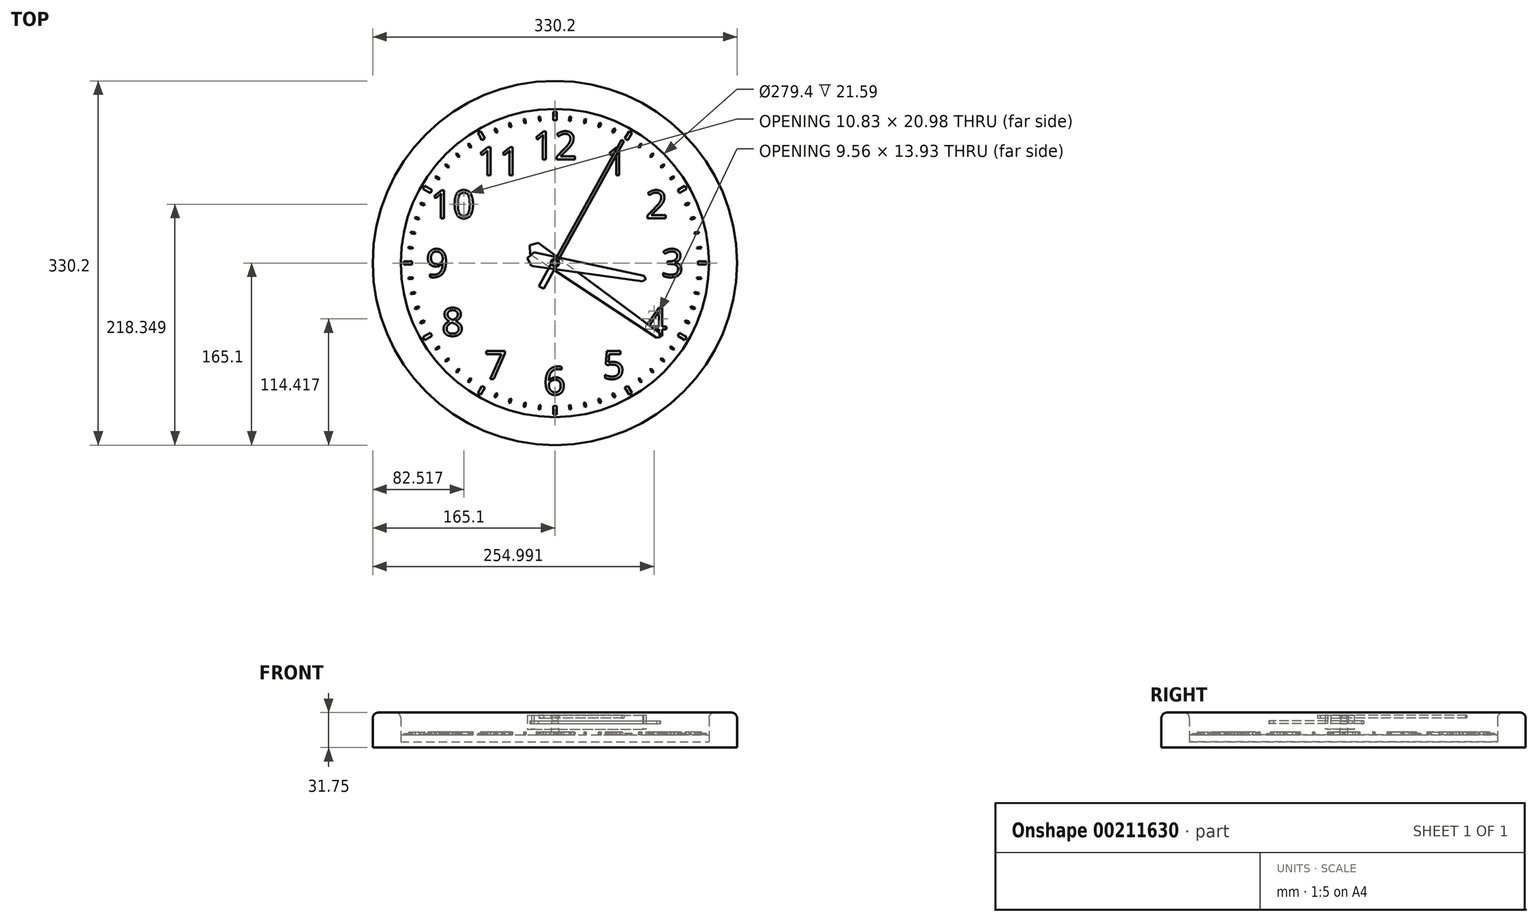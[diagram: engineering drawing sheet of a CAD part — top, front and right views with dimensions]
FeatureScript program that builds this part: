
annotation { "Feature Type Name" : "Feature", "Feature Type Description" : "" }
export const myFeature = defineFeature(function(context is Context, id is Id, definition is map)
    precondition{}
    {
        {
            var Q0;
            Q0=qCreatedBy(makeId("Front.planeOp"),FACE);
            var sketch = newSketch(context, id + "F0", { "sketchPlane" : qUnion([Q0])});
            skLineSegment(sketch, "E0", {"start": v(0, 0) * mm, "end": v(0, 54.8) * mm, "construction": true});
            skLineSegment(sketch, "E1.bottom", {"start": v(139.7, 0) * mm, "end": v(165.1, 0) * mm});
            skLineSegment(sketch, "E1.top", {"start": v(139.7, 31.75) * mm, "end": v(165.1, 31.75) * mm});
            skLineSegment(sketch, "E1.left", {"start": v(139.7, 5.08) * mm, "end": v(139.7, 31.75) * mm});
            skLineSegment(sketch, "E1.right", {"start": v(165.1, 0) * mm, "end": v(165.1, 31.75) * mm});
            skLineSegment(sketch, "E2", {"start": v(152.4, 0) * mm, "end": v(152.4, 31.75) * mm, "construction": true});
            skLineSegment(sketch, "E3.bottom", {"start": v(0, 0) * mm, "end": v(139.7, 0) * mm});
            skLineSegment(sketch, "E3.top", {"start": v(0, 5.08) * mm, "end": v(139.7, 5.08) * mm});
            skLineSegment(sketch, "E3.left", {"start": v(0, 0) * mm, "end": v(0, 5.08) * mm});
            skSolve(sketch);
        }
        {
            var Q0;
            Q0=makeQuery(id+"F0.imprint","IMPRINT",FACE,{"disambiguationData":[TD([[makeQuery(id+"F0.imprint","IMPRINT",EDGE,{"derivedFrom":sQuery(id+"F0.wireOp",EDGE,"E1.bottom")}),1.0]])]});
            var Q1;
            Q1=sQuery(id+"F0.wireOp",EDGE,"E0");
            revolve(context, id + "F1", {"entities" : qUnion([Q0]), "axis" : qUnion([Q1]), "revolveType" : RevolveType.FULL});
        }
        {
            var Q0;
            Q0=makeQuery(id+"F1.opRevolve","SWEPT_EDGE",EDGE,{"disambiguationData":[OSD([sQuery(id+"F0.wireOp",EDGE,"E1.top"),sQuery(id+"F0.wireOp",EDGE,"E1.left")])]});
            var Q1;
            Q1=makeQuery(id+"F1.opRevolve","SWEPT_EDGE",EDGE,{"disambiguationData":[OSD([sQuery(id+"F0.wireOp",EDGE,"E1.top"),sQuery(id+"F0.wireOp",EDGE,"E1.right")])]});
            fillet(context, id + "F2", {"entities" : qUnion([Q0, Q1]), "radius" : 5.08 * mm, "tangentPropagation" : true, "allowEdgeOverflow" : false});
        }
        {
            var Q0;
            Q0=makeQuery(id+"F1.opRevolve","SWEPT_FACE",FACE,{"disambiguationData":[OSD([sQuery(id+"F0.wireOp",EDGE,"E3.top")])]});
            extrude(context, id + "F3", {"entities" : qUnion([Q0]), "depth" : 6.35 * mm});
        }
        {
            var Q0;
            Q0=makeQuery(id+"F3.opExtrude","CAP_FACE",FACE,{"disambiguationData":[OSD([sQuery(id+"F0.wireOp",EDGE,"E3.top")])],"isStart":false});
            var sketch = newSketch(context, id + "F4", { "sketchPlane" : qUnion([Q0])});
            skText(sketch, "E4", { "text": "12", "fontName": "OpenSans-Regular.ttf"});
            skLineSegment(sketch, "E5", {"start": v(0, 0) * mm, "end": v(0, 106.68) * mm, "construction": true});
            skLineSegment(sketch, "E6.1.0", {"start": v(0, 0) * mm, "end": v(-53.34, 92.39) * mm, "construction": true});
            skLineSegment(sketch, "E6.2.0", {"start": v(0, 0) * mm, "end": v(-92.39, 53.34) * mm, "construction": true});
            skLineSegment(sketch, "E6.3.0", {"start": v(0, 0) * mm, "end": v(-106.68, 0) * mm, "construction": true});
            skLineSegment(sketch, "E6.4.0", {"start": v(0, 0) * mm, "end": v(-92.39, -53.34) * mm, "construction": true});
            skLineSegment(sketch, "E6.5.0", {"start": v(0, 0) * mm, "end": v(-53.34, -92.39) * mm, "construction": true});
            skLineSegment(sketch, "E6.6.0", {"start": v(0, 0) * mm, "end": v(0, -106.68) * mm, "construction": true});
            skLineSegment(sketch, "E6.7.0", {"start": v(0, 0) * mm, "end": v(53.34, -92.39) * mm, "construction": true});
            skLineSegment(sketch, "E6.8.0", {"start": v(0, 0) * mm, "end": v(92.39, -53.34) * mm, "construction": true});
            skLineSegment(sketch, "E6.9.0", {"start": v(0, 0) * mm, "end": v(106.68, 0) * mm, "construction": true});
            skLineSegment(sketch, "E6.10.0", {"start": v(0, 0) * mm, "end": v(92.39, 53.34) * mm, "construction": true});
            skLineSegment(sketch, "E6.11.0", {"start": v(0, 0) * mm, "end": v(53.34, 92.39) * mm, "construction": true});
            skPoint(sketch, "E6.center", {"position": v(0, 0) * mm});
            skText(sketch, "E7", { "text": "2", "fontName": "OpenSans-Regular.ttf"});
            skText(sketch, "E8", { "text": "3", "fontName": "OpenSans-Regular.ttf"});
            skText(sketch, "E9", { "text": "4", "fontName": "OpenSans-Regular.ttf"});
            skText(sketch, "E10", { "text": "1", "fontName": "OpenSans-Regular.ttf"});
            skText(sketch, "E11", { "text": "5", "fontName": "OpenSans-Regular.ttf"});
            skText(sketch, "E12", { "text": "6", "fontName": "OpenSans-Regular.ttf"});
            skText(sketch, "E13", { "text": "7", "fontName": "OpenSans-Regular.ttf"});
            skText(sketch, "E14", { "text": "9", "fontName": "OpenSans-Regular.ttf"});
            skText(sketch, "E15", { "text": "8", "fontName": "OpenSans-Regular.ttf"});
            skText(sketch, "E16", { "text": "10", "fontName": "OpenSans-Regular.ttf"});
            skText(sketch, "E17", { "text": "11", "fontName": "OpenSans-Regular.ttf"});
            const initialGuessF4  = {"E4": [-0.02037, 0.09398, 1, 0, 0.0254], "E7": [0.0821, 0.04064, 1, 0, 0.0254], "E8": [0.09649, -0.0127, 1, 0, 0.0254], "E9": [0.08151, -0.06604, 1, 0, 0.0254], "E10": [0.04604, 0.07969, 1, 0, 0.0254], "E11": [0.04313, -0.10509, 1, 0, 0.0254], "E12": [-0.01037, -0.11938, 1, 0, 0.0254], "E13": [-0.06367, -0.10509, 1, 0, 0.0254], "E14": [-0.11696, -0.0127, 1, 0, 0.0254], "E15": [-0.1027, -0.06604, 1, 0, 0.0254], "E16": [-0.11282, 0.04064, 1, 0, 0.0254], "E17": [-0.07073, 0.07969, 1, 0, 0.0254]};
            skSetInitialGuess(sketch, initialGuessF4);
            skSolve(sketch);
        }
        {
            var Q0;
            Q0=qSketchRegion(id+"F4",true);
            extrude(context, id + "F5", {"entities" : qUnion([Q0]), "depth" : 2.54 * mm});
        }
        {
            var Q0;
            Q0=makeQuery(id+"F3.opExtrude","CAP_FACE",FACE,{"disambiguationData":[OSD([sQuery(id+"F0.wireOp",EDGE,"E3.top")])],"isStart":false});
            cPlane(context, id + "F6", {"entities" : qUnion([Q0]), "cplaneType" : CPlaneType.OFFSET, "offset" : 5.08 * mm, "width" : 152.4 * mm, "height" : 152.4 * mm});
        }
        {
            var Q0;
            Q0=qCreatedBy(id+"F6.planeOp",FACE);
            var sketch = newSketch(context, id + "F7", { "sketchPlane" : qUnion([Q0])});
            skLineSegment(sketch, "E18", {"start": v(5, -0.88) * mm, "end": v(80.05, -14.11) * mm, "construction": true});
            skLineSegment(sketch, "E19", {"start": v(80.05, -14.11) * mm, "end": v(79.6, -16.62) * mm, "construction": true});
            skLineSegment(sketch, "E20", {"start": v(-20.01, 3.53) * mm, "end": v(-21.11, -2.72) * mm, "construction": true});
            skLineSegment(sketch, "E21", {"start": v(5, -0.88) * mm, "end": v(-25.01, 4.41) * mm, "construction": true});
            skLineSegment(sketch, "E22", {"start": v(-25.01, 4.41) * mm, "end": v(-21.11, -2.72) * mm});
            skLineSegment(sketch, "E23", {"start": v(-21.11, -2.72) * mm, "end": v(79.6, -16.62) * mm});
            skLineSegment(sketch, "E24", {"start": v(80.05, -14.11) * mm, "end": v(82.55, -14.56) * mm, "construction": true});
            skLineSegment(sketch, "E25", {"start": v(82.55, -14.56) * mm, "end": v(79.6, -16.62) * mm});
            skLineSegment(sketch, "E26.MirrorCS", {"start": v(82.55, -14.56) * mm, "end": v(80.49, -11.61) * mm});
            skLineSegment(sketch, "E27.MirrorCS", {"start": v(-18.9, 9.78) * mm, "end": v(80.49, -11.61) * mm});
            skLineSegment(sketch, "E28.MirrorCS", {"start": v(-25.01, 4.41) * mm, "end": v(-18.9, 9.78) * mm});
            skSolve(sketch);
        }
        {
            var Q0;
            Q0=makeQuery(id+"F7.imprint","IMPRINT",FACE,{"disambiguationData":[TD([[makeQuery(id+"F7.imprint","IMPRINT",EDGE,{"derivedFrom":sQuery(id+"F7.wireOp",EDGE,"E22")}),1.0]])]});
            extrude(context, id + "F8", {"entities" : qUnion([Q0]), "depth" : 12.7 * mm});
        }
        {
            var Q0;
            Q0=makeQuery(id+"F3.opExtrude","CAP_FACE",FACE,{"disambiguationData":[OSD([sQuery(id+"F0.wireOp",EDGE,"E3.top")])],"isStart":false});
            cPlane(context, id + "F9", {"entities" : qUnion([Q0]), "cplaneType" : CPlaneType.OFFSET, "offset" : 10.16 * mm, "width" : 152.4 * mm, "height" : 152.4 * mm});
        }
        {
            var Q0;
            Q0=qCreatedBy(id+"F9.planeOp",FACE);
            var sketch = newSketch(context, id + "F10", { "sketchPlane" : qUnion([Q0])});
            skLineSegment(sketch, "E29", {"start": v(0, 0) * mm, "end": v(95.7, -67.02) * mm, "construction": true});
            skLineSegment(sketch, "E30", {"start": v(0, 0) * mm, "end": v(-22.89, 16.03) * mm, "construction": true});
            skLineSegment(sketch, "E31", {"start": v(-18.73, 13.11) * mm, "end": v(-15.08, 18.31) * mm, "construction": true});
            skLineSegment(sketch, "E32", {"start": v(93.63, -65.56) * mm, "end": v(95.09, -63.48) * mm, "construction": true});
            skLineSegment(sketch, "E33", {"start": v(-22.89, 16.03) * mm, "end": v(-15.08, 18.31) * mm});
            skLineSegment(sketch, "E34", {"start": v(-15.08, 18.31) * mm, "end": v(95.09, -63.48) * mm});
            skLineSegment(sketch, "E35", {"start": v(95.09, -63.48) * mm, "end": v(95.7, -67.02) * mm});
            skLineSegment(sketch, "E36.MirrorCS", {"start": v(-22.89, 16.03) * mm, "end": v(-22.37, 7.91) * mm});
            skLineSegment(sketch, "E37.MirrorCS", {"start": v(-22.37, 7.91) * mm, "end": v(92.17, -67.64) * mm});
            skLineSegment(sketch, "E38.MirrorCS", {"start": v(92.17, -67.64) * mm, "end": v(95.7, -67.02) * mm});
            skLineSegment(sketch, "E39", {"start": v(0, 0) * mm, "end": v(0, -35.35) * mm, "construction": true});
            skSolve(sketch);
        }
        {
            var Q0;
            Q0=makeQuery(id+"F10.imprint","IMPRINT",FACE,{"disambiguationData":[TD([[makeQuery(id+"F10.imprint","IMPRINT",EDGE,{"derivedFrom":sQuery(id+"F10.wireOp",EDGE,"E33")}),-1.0]])]});
            extrude(context, id + "F11", {"entities" : qUnion([Q0]), "depth" : 2.54 * mm});
        }
        {
            var Q0;
            Q0=makeQuery(id+"F3.opExtrude","CAP_FACE",FACE,{"disambiguationData":[OSD([sQuery(id+"F0.wireOp",EDGE,"E3.top")])],"isStart":false});
            cPlane(context, id + "F12", {"entities" : qUnion([Q0]), "cplaneType" : CPlaneType.OFFSET, "offset" : 15.24 * mm, "width" : 152.4 * mm, "height" : 152.4 * mm});
        }
        {
            var Q0;
            Q0=qCreatedBy(id+"F12.planeOp",FACE);
            var sketch = newSketch(context, id + "F13", { "sketchPlane" : qUnion([Q0])});
            skArc(sketch, "E40", {"start": v(0.85, -3.72) * mm, "mid": v(3.63, -1.17) * mm, "end": v(2.85, 2.53) * mm});
            skLineSegment(sketch, "E41", {"start": v(0, 0) * mm, "end": v(61.55, 111.09) * mm, "construction": true});
            skLineSegment(sketch, "E42", {"start": v(0, 0) * mm, "end": v(-12.31, -22.22) * mm, "construction": true});
            skLineSegment(sketch, "E43", {"start": v(-12.31, -22.22) * mm, "end": v(-10.09, -23.45) * mm});
            skLineSegment(sketch, "E44", {"start": v(-10.09, -23.45) * mm, "end": v(0.85, -3.72) * mm});
            skLineSegment(sketch, "E45", {"start": v(61.55, 111.09) * mm, "end": v(62.66, 110.47) * mm});
            skLineSegment(sketch, "E46", {"start": v(62.66, 110.47) * mm, "end": v(2.85, 2.53) * mm});
            skLineSegment(sketch, "E47.MirrorCS", {"start": v(61.55, 111.09) * mm, "end": v(60.44, 111.7) * mm});
            skLineSegment(sketch, "E48.MirrorCS", {"start": v(60.44, 111.7) * mm, "end": v(0.63, 3.76) * mm});
            skArc(sketch, "E49.MirrorCS", {"start": v(-3.6, -1.25) * mm, "mid": v(-2.91, 2.46) * mm, "end": v(0.63, 3.76) * mm});
            skLineSegment(sketch, "E50.MirrorCS", {"start": v(-14.53, -20.99) * mm, "end": v(-3.6, -1.25) * mm});
            skLineSegment(sketch, "E51.MirrorCS", {"start": v(-12.31, -22.22) * mm, "end": v(-14.53, -20.99) * mm});
            skSolve(sketch);
        }
        {
            var Q0;
            Q0=makeQuery(id+"F13.imprint","IMPRINT",FACE,{"disambiguationData":[TD([[makeQuery(id+"F13.imprint","IMPRINT",EDGE,{"derivedFrom":sQuery(id+"F13.wireOp",EDGE,"E40")}),1.0]])]});
            extrude(context, id + "F14", {"entities" : qUnion([Q0]), "depth" : 2.54 * mm});
        }
        {
            var Q0;
            Q0=makeQuery(id+"F3.opExtrude","CAP_FACE",FACE,{"disambiguationData":[OSD([sQuery(id+"F0.wireOp",EDGE,"E3.top")])],"isStart":false});
            var sketch = newSketch(context, id + "F15", { "sketchPlane" : qUnion([Q0])});
            skCircle(sketch, "E52", {"center": v(0, 0) * mm, "radius": 3.81 * mm});
            skSolve(sketch);
        }
        {
            var Q0;
            Q0=makeQuery(id+"F14.opExtrude","CAP_FACE",FACE,{"disambiguationData":[OSD([sQuery(id+"F13.wireOp",EDGE,"E40"),sQuery(id+"F13.wireOp",EDGE,"E43"),sQuery(id+"F13.wireOp",EDGE,"E44"),sQuery(id+"F13.wireOp",EDGE,"E45"),sQuery(id+"F13.wireOp",EDGE,"E46"),sQuery(id+"F13.wireOp",EDGE,"E47.MirrorCS"),sQuery(id+"F13.wireOp",EDGE,"E48.MirrorCS"),sQuery(id+"F13.wireOp",EDGE,"E49.MirrorCS"),sQuery(id+"F13.wireOp",EDGE,"E50.MirrorCS"),sQuery(id+"F13.wireOp",EDGE,"E51.MirrorCS")])],"isStart":false});
            var sketch = newSketch(context, id + "F16", { "sketchPlane" : qUnion([Q0])});
            skCircle(sketch, "E53", {"center": v(0, 0) * mm, "radius": 2.54 * mm});
            skSolve(sketch);
        }
        {
            var Q1;
            Q1=makeQuery(id+"F15.imprint","IMPRINT",FACE,{"disambiguationData":[TD([[makeQuery(id+"F15.imprint","IMPRINT",EDGE,{"derivedFrom":sQuery(id+"F15.wireOp",EDGE,"E52")}),1.0]])]});
            var Q2;
            Q2=makeQuery(id+"F16.imprint","IMPRINT",FACE,{"disambiguationData":[TD([[makeQuery(id+"F16.imprint","IMPRINT",EDGE,{"derivedFrom":sQuery(id+"F16.wireOp",EDGE,"E53")}),1.0]])]});
            loft(context, id + "F17", {"sheetProfilesArray" : [{ "sheetProfileEntities" : qUnion([Q1]) }, { "sheetProfileEntities" : qUnion([Q2]) }]});
        }
        {
            var Q0;
            Q0=makeQuery(id+"F17.opLoft","SWEPT_BODY",BODY,{"disambiguationData":[OSD([makeQuery(id+"F15.imprint","IMPRINT",FACE,{"disambiguationData":[TD([[makeQuery(id+"F15.imprint","IMPRINT",EDGE,{"derivedFrom":sQuery(id+"F15.wireOp",EDGE,"E52")}),1.0]])]}),makeQuery(id+"F16.imprint","IMPRINT",FACE,{"disambiguationData":[TD([[makeQuery(id+"F16.imprint","IMPRINT",EDGE,{"derivedFrom":sQuery(id+"F16.wireOp",EDGE,"E53")}),1.0]])]})])]});
            var Q1;
            Q1=makeQuery(id+"F8.opExtrude","SWEPT_BODY",BODY,{"disambiguationData":[OSD([sQuery(id+"F7.wireOp",EDGE,"E22"),sQuery(id+"F7.wireOp",EDGE,"E23"),sQuery(id+"F7.wireOp",EDGE,"E25"),sQuery(id+"F7.wireOp",EDGE,"E26.MirrorCS"),sQuery(id+"F7.wireOp",EDGE,"E27.MirrorCS"),sQuery(id+"F7.wireOp",EDGE,"E28.MirrorCS")])]});
            booleanBodies(context, id + "F18", {"operationType" : BooleanOperationType.SUBTRACTION, "tools" : qUnion([Q0]), "targets" : qUnion([Q1]), "keepTools" : true});
        }
        {
            var Q0;
            Q0=makeQuery(id+"F17.opLoft","SWEPT_BODY",BODY,{"disambiguationData":[OSD([makeQuery(id+"F15.imprint","IMPRINT",FACE,{"disambiguationData":[TD([[makeQuery(id+"F15.imprint","IMPRINT",EDGE,{"derivedFrom":sQuery(id+"F15.wireOp",EDGE,"E52")}),1.0]])]}),makeQuery(id+"F16.imprint","IMPRINT",FACE,{"disambiguationData":[TD([[makeQuery(id+"F16.imprint","IMPRINT",EDGE,{"derivedFrom":sQuery(id+"F16.wireOp",EDGE,"E53")}),1.0]])]})])]});
            var Q1;
            Q1=makeQuery(id+"F11.opExtrude","SWEPT_BODY",BODY,{"disambiguationData":[OSD([sQuery(id+"F10.wireOp",EDGE,"E33"),sQuery(id+"F10.wireOp",EDGE,"E34"),sQuery(id+"F10.wireOp",EDGE,"E35"),sQuery(id+"F10.wireOp",EDGE,"E36.MirrorCS"),sQuery(id+"F10.wireOp",EDGE,"E37.MirrorCS"),sQuery(id+"F10.wireOp",EDGE,"E38.MirrorCS")])]});
            booleanBodies(context, id + "F19", {"operationType" : BooleanOperationType.SUBTRACTION, "tools" : qUnion([Q0]), "targets" : qUnion([Q1]), "keepTools" : true});
        }
        {
            var Q0;
            Q0=makeQuery(id+"F17.opLoft","SWEPT_BODY",BODY,{"disambiguationData":[OSD([makeQuery(id+"F15.imprint","IMPRINT",FACE,{"disambiguationData":[TD([[makeQuery(id+"F15.imprint","IMPRINT",EDGE,{"derivedFrom":sQuery(id+"F15.wireOp",EDGE,"E52")}),1.0]])]}),makeQuery(id+"F16.imprint","IMPRINT",FACE,{"disambiguationData":[TD([[makeQuery(id+"F16.imprint","IMPRINT",EDGE,{"derivedFrom":sQuery(id+"F16.wireOp",EDGE,"E53")}),1.0]])]})])]});
            var Q1;
            Q1=makeQuery(id+"F14.opExtrude","SWEPT_BODY",BODY,{"disambiguationData":[OSD([sQuery(id+"F13.wireOp",EDGE,"E40"),sQuery(id+"F13.wireOp",EDGE,"E43"),sQuery(id+"F13.wireOp",EDGE,"E44"),sQuery(id+"F13.wireOp",EDGE,"E45"),sQuery(id+"F13.wireOp",EDGE,"E46"),sQuery(id+"F13.wireOp",EDGE,"E47.MirrorCS"),sQuery(id+"F13.wireOp",EDGE,"E48.MirrorCS"),sQuery(id+"F13.wireOp",EDGE,"E49.MirrorCS"),sQuery(id+"F13.wireOp",EDGE,"E50.MirrorCS"),sQuery(id+"F13.wireOp",EDGE,"E51.MirrorCS")])]});
            booleanBodies(context, id + "F20", {"operationType" : BooleanOperationType.SUBTRACTION, "tools" : qUnion([Q0]), "targets" : qUnion([Q1]), "keepTools" : true});
        }
        {
            var Q0;
            Q0=makeQuery(id+"F18.opBoolean","INTERSECT",EDGE,{"derivedFrom":[makeQuery(id+"F17.opLoft","SWEPT_FACE",FACE,{"disambiguationData":[OSD([sQuery(id+"F15.wireOp",EDGE,"E52"),sQuery(id+"F16.wireOp",EDGE,"E53")])]}),makeQuery(id+"F8.opExtrude","CAP_FACE",FACE,{"disambiguationData":[OSD([sQuery(id+"F7.wireOp",EDGE,"E22"),sQuery(id+"F7.wireOp",EDGE,"E23"),sQuery(id+"F7.wireOp",EDGE,"E25"),sQuery(id+"F7.wireOp",EDGE,"E26.MirrorCS"),sQuery(id+"F7.wireOp",EDGE,"E27.MirrorCS"),sQuery(id+"F7.wireOp",EDGE,"E28.MirrorCS")])],"isStart":true})]});
            var Q1;
            Q1=makeQuery(id+"F18.opBoolean","INTERSECT",EDGE,{"derivedFrom":[makeQuery(id+"F17.opLoft","SWEPT_FACE",FACE,{"disambiguationData":[OSD([sQuery(id+"F15.wireOp",EDGE,"E52"),sQuery(id+"F16.wireOp",EDGE,"E53")])]}),makeQuery(id+"F8.opExtrude","CAP_FACE",FACE,{"disambiguationData":[OSD([sQuery(id+"F7.wireOp",EDGE,"E22"),sQuery(id+"F7.wireOp",EDGE,"E23"),sQuery(id+"F7.wireOp",EDGE,"E25"),sQuery(id+"F7.wireOp",EDGE,"E26.MirrorCS"),sQuery(id+"F7.wireOp",EDGE,"E27.MirrorCS"),sQuery(id+"F7.wireOp",EDGE,"E28.MirrorCS")])],"isStart":false})]});
            var Q2;
            Q2=makeQuery(id+"F19.opBoolean","INTERSECT",EDGE,{"derivedFrom":[makeQuery(id+"F17.opLoft","SWEPT_FACE",FACE,{"disambiguationData":[OSD([sQuery(id+"F15.wireOp",EDGE,"E52"),sQuery(id+"F16.wireOp",EDGE,"E53")])]}),makeQuery(id+"F11.opExtrude","CAP_FACE",FACE,{"disambiguationData":[OSD([sQuery(id+"F10.wireOp",EDGE,"E33"),sQuery(id+"F10.wireOp",EDGE,"E34"),sQuery(id+"F10.wireOp",EDGE,"E35"),sQuery(id+"F10.wireOp",EDGE,"E36.MirrorCS"),sQuery(id+"F10.wireOp",EDGE,"E37.MirrorCS"),sQuery(id+"F10.wireOp",EDGE,"E38.MirrorCS")])],"isStart":true})]});
            var Q3;
            Q3=makeQuery(id+"F19.opBoolean","INTERSECT",EDGE,{"derivedFrom":[makeQuery(id+"F17.opLoft","SWEPT_FACE",FACE,{"disambiguationData":[OSD([sQuery(id+"F15.wireOp",EDGE,"E52"),sQuery(id+"F16.wireOp",EDGE,"E53")])]}),makeQuery(id+"F11.opExtrude","CAP_FACE",FACE,{"disambiguationData":[OSD([sQuery(id+"F10.wireOp",EDGE,"E33"),sQuery(id+"F10.wireOp",EDGE,"E34"),sQuery(id+"F10.wireOp",EDGE,"E35"),sQuery(id+"F10.wireOp",EDGE,"E36.MirrorCS"),sQuery(id+"F10.wireOp",EDGE,"E37.MirrorCS"),sQuery(id+"F10.wireOp",EDGE,"E38.MirrorCS")])],"isStart":false})]});
            var Q4;
            Q4=makeQuery(id+"F20.opBoolean","INTERSECT",EDGE,{"derivedFrom":[makeQuery(id+"F17.opLoft","SWEPT_FACE",FACE,{"disambiguationData":[OSD([sQuery(id+"F15.wireOp",EDGE,"E52"),sQuery(id+"F16.wireOp",EDGE,"E53")])]}),makeQuery(id+"F14.opExtrude","CAP_FACE",FACE,{"disambiguationData":[OSD([sQuery(id+"F13.wireOp",EDGE,"E40"),sQuery(id+"F13.wireOp",EDGE,"E43"),sQuery(id+"F13.wireOp",EDGE,"E44"),sQuery(id+"F13.wireOp",EDGE,"E45"),sQuery(id+"F13.wireOp",EDGE,"E46"),sQuery(id+"F13.wireOp",EDGE,"E47.MirrorCS"),sQuery(id+"F13.wireOp",EDGE,"E48.MirrorCS"),sQuery(id+"F13.wireOp",EDGE,"E49.MirrorCS"),sQuery(id+"F13.wireOp",EDGE,"E50.MirrorCS"),sQuery(id+"F13.wireOp",EDGE,"E51.MirrorCS")])],"isStart":true})]});
            var Q5;
            Q5=makeQuery(id+"F20.opBoolean","COPY",EDGE,{"derivedFrom":makeQuery(id+"F17.opLoft","MID_CAP_EDGE",EDGE,{"disambiguationData":[OSD([sQuery(id+"F15.wireOp",EDGE,"E52"),sQuery(id+"F16.wireOp",EDGE,"E53")])],"capPos":1.0})});
            chamfer(context, id + "F21", {"entities" : qUnion([Q0, Q1, Q2, Q3, Q4, Q5]), "width" : 0.25 * mm, "tangentPropagation" : true});
        }
        {
            var Q0;
            Q0=makeQuery(id+"F3.opExtrude","CAP_FACE",FACE,{"disambiguationData":[OSD([sQuery(id+"F0.wireOp",EDGE,"E3.top")])],"isStart":false});
            var sketch = newSketch(context, id + "F22", { "sketchPlane" : qUnion([Q0])});
            skLineSegment(sketch, "E54", {"start": v(0, 0) * mm, "end": v(0, 139.7) * mm, "construction": true});
            skLineSegment(sketch, "E55.bottom", {"start": v(1.52, 137.16) * mm, "end": v(-1.52, 137.16) * mm});
            skLineSegment(sketch, "E55.top", {"start": v(1.52, 129.54) * mm, "end": v(-1.52, 129.54) * mm});
            skLineSegment(sketch, "E55.left", {"start": v(1.52, 137.16) * mm, "end": v(1.52, 129.54) * mm});
            skLineSegment(sketch, "E55.right", {"start": v(-1.52, 137.16) * mm, "end": v(-1.52, 129.54) * mm});
            skPoint(sketch, "E55.middle", {"position": v(0, 133.35) * mm});
            skSolve(sketch);
        }
        {
            var Q0;
            Q0=makeQuery(id+"F22.imprint","IMPRINT",FACE,{"disambiguationData":[TD([[makeQuery(id+"F22.imprint","IMPRINT",EDGE,{"derivedFrom":sQuery(id+"F22.wireOp",EDGE,"E55.bottom")}),1.0]])]});
            extrude(context, id + "F23", {"entities" : qUnion([Q0]), "depth" : 1.27 * mm});
        }
        {
            var Q0;
            Q0=makeQuery(id+"F23.opExtrude","SWEPT_BODY",BODY,{"disambiguationData":[OSD([sQuery(id+"F22.wireOp",EDGE,"E55.bottom"),sQuery(id+"F22.wireOp",EDGE,"E55.top"),sQuery(id+"F22.wireOp",EDGE,"E55.left"),sQuery(id+"F22.wireOp",EDGE,"E55.right")])]});
            var Q1;
            Q1=sQuery(id+"F0.wireOp",EDGE,"E0");
            circularPattern(context, id + "F24", {"entities" : qUnion([Q0]), "axis" : qUnion([Q1]), "angle" : 360 * degree, "instanceCount" : 12, "equalSpace" : true});
        }
        {
            var Q0;
            Q0=makeQuery(id+"F3.opExtrude","CAP_FACE",FACE,{"disambiguationData":[OSD([sQuery(id+"F0.wireOp",EDGE,"E3.top")])],"isStart":false});
            var sketch = newSketch(context, id + "F25", { "sketchPlane" : qUnion([Q0])});
            skLineSegment(sketch, "E56", {"start": v(0, 0) * mm, "end": v(0, 65.46) * mm, "construction": true});
            skLineSegment(sketch, "E57", {"start": v(0, 0) * mm, "end": v(13.94, 132.62) * mm, "construction": true});
            skLineSegment(sketch, "E58", {"start": v(13.54, 128.83) * mm, "end": v(14.3, 128.75) * mm});
            skLineSegment(sketch, "E59", {"start": v(13.94, 132.62) * mm, "end": v(14.7, 132.54) * mm});
            skLineSegment(sketch, "E60", {"start": v(14.7, 132.54) * mm, "end": v(14.3, 128.75) * mm});
            skLineSegment(sketch, "E61.MirrorCS", {"start": v(13.94, 132.62) * mm, "end": v(13.18, 132.7) * mm});
            skLineSegment(sketch, "E62.MirrorCS", {"start": v(13.18, 132.7) * mm, "end": v(12.78, 128.91) * mm});
            skLineSegment(sketch, "E63.MirrorCS", {"start": v(13.54, 128.83) * mm, "end": v(12.78, 128.91) * mm});
            skLineSegment(sketch, "E64.2.0", {"start": v(-13.18, 132.7) * mm, "end": v(-12.78, 128.91) * mm});
            skLineSegment(sketch, "E64.2.1", {"start": v(-13.94, 132.62) * mm, "end": v(-13.18, 132.7) * mm});
            skLineSegment(sketch, "E64.2.2", {"start": v(-13.94, 132.62) * mm, "end": v(-14.7, 132.54) * mm});
            skLineSegment(sketch, "E64.2.3", {"start": v(-14.7, 132.54) * mm, "end": v(-14.3, 128.75) * mm});
            skLineSegment(sketch, "E64.2.4", {"start": v(-13.54, 128.83) * mm, "end": v(-14.3, 128.75) * mm});
            skLineSegment(sketch, "E64.2.5", {"start": v(-13.54, 128.83) * mm, "end": v(-12.78, 128.91) * mm});
            skLineSegment(sketch, "E64.3.0", {"start": v(-26.98, 130.6) * mm, "end": v(-26.19, 126.87) * mm});
            skLineSegment(sketch, "E64.3.1", {"start": v(-27.73, 130.44) * mm, "end": v(-26.98, 130.6) * mm});
            skLineSegment(sketch, "E64.3.2", {"start": v(-27.73, 130.44) * mm, "end": v(-28.47, 130.28) * mm});
            skLineSegment(sketch, "E64.3.3", {"start": v(-28.47, 130.28) * mm, "end": v(-27.68, 126.55) * mm});
            skLineSegment(sketch, "E64.3.4", {"start": v(-26.93, 126.7) * mm, "end": v(-27.68, 126.55) * mm});
            skLineSegment(sketch, "E64.3.5", {"start": v(-26.93, 126.7) * mm, "end": v(-26.19, 126.87) * mm});
            skLineSegment(sketch, "E64.4.0", {"start": v(-40.48, 127.06) * mm, "end": v(-39.3, 123.44) * mm});
            skLineSegment(sketch, "E64.4.1", {"start": v(-41.2, 126.82) * mm, "end": v(-40.48, 127.06) * mm});
            skLineSegment(sketch, "E64.4.2", {"start": v(-41.2, 126.82) * mm, "end": v(-41.93, 126.59) * mm});
            skLineSegment(sketch, "E64.4.3", {"start": v(-41.93, 126.59) * mm, "end": v(-40.75, 122.96) * mm});
            skLineSegment(sketch, "E64.4.4", {"start": v(-40.03, 123.2) * mm, "end": v(-40.75, 122.96) * mm});
            skLineSegment(sketch, "E64.4.5", {"start": v(-40.03, 123.2) * mm, "end": v(-39.3, 123.44) * mm});
            skLineSegment(sketch, "E64.5.0", {"start": v(-53.54, 122.13) * mm, "end": v(-52, 118.65) * mm});
            skLineSegment(sketch, "E64.5.1", {"start": v(-54.24, 121.82) * mm, "end": v(-53.54, 122.13) * mm});
            skLineSegment(sketch, "E64.5.2", {"start": v(-54.24, 121.82) * mm, "end": v(-54.93, 121.51) * mm});
            skLineSegment(sketch, "E64.5.3", {"start": v(-54.93, 121.51) * mm, "end": v(-53.38, 118.03) * mm});
            skLineSegment(sketch, "E64.5.4", {"start": v(-52.69, 118.34) * mm, "end": v(-53.38, 118.03) * mm});
            skLineSegment(sketch, "E64.5.5", {"start": v(-52.69, 118.34) * mm, "end": v(-52, 118.65) * mm});
            skLineSegment(sketch, "E64.7.0", {"start": v(-77.76, 108.33) * mm, "end": v(-75.53, 105.25) * mm});
            skLineSegment(sketch, "E64.7.1", {"start": v(-78.38, 107.88) * mm, "end": v(-77.76, 108.33) * mm});
            skLineSegment(sketch, "E64.7.2", {"start": v(-78.38, 107.88) * mm, "end": v(-79, 107.43) * mm});
            skLineSegment(sketch, "E64.7.3", {"start": v(-79, 107.43) * mm, "end": v(-76.76, 104.35) * mm});
            skLineSegment(sketch, "E64.7.4", {"start": v(-76.14, 104.8) * mm, "end": v(-76.76, 104.35) * mm});
            skLineSegment(sketch, "E64.7.5", {"start": v(-76.14, 104.8) * mm, "end": v(-75.53, 105.25) * mm});
            skLineSegment(sketch, "E64.8.0", {"start": v(-88.66, 99.6) * mm, "end": v(-86.11, 96.78) * mm});
            skLineSegment(sketch, "E64.8.1", {"start": v(-89.23, 99.1) * mm, "end": v(-88.66, 99.6) * mm});
            skLineSegment(sketch, "E64.8.2", {"start": v(-89.23, 99.1) * mm, "end": v(-89.8, 98.59) * mm});
            skLineSegment(sketch, "E64.8.3", {"start": v(-89.8, 98.59) * mm, "end": v(-87.25, 95.76) * mm});
            skLineSegment(sketch, "E64.8.4", {"start": v(-86.68, 96.27) * mm, "end": v(-87.25, 95.76) * mm});
            skLineSegment(sketch, "E64.8.5", {"start": v(-86.68, 96.27) * mm, "end": v(-86.11, 96.78) * mm});
            skLineSegment(sketch, "E64.9.0", {"start": v(-98.59, 89.8) * mm, "end": v(-95.76, 87.25) * mm});
            skLineSegment(sketch, "E64.9.1", {"start": v(-99.1, 89.23) * mm, "end": v(-98.59, 89.8) * mm});
            skLineSegment(sketch, "E64.9.2", {"start": v(-99.1, 89.23) * mm, "end": v(-99.6, 88.66) * mm});
            skLineSegment(sketch, "E64.9.3", {"start": v(-99.6, 88.66) * mm, "end": v(-96.78, 86.11) * mm});
            skLineSegment(sketch, "E64.9.4", {"start": v(-96.27, 86.68) * mm, "end": v(-96.78, 86.11) * mm});
            skLineSegment(sketch, "E64.9.5", {"start": v(-96.27, 86.68) * mm, "end": v(-95.76, 87.25) * mm});
            skLineSegment(sketch, "E64.10.0", {"start": v(-107.43, 79) * mm, "end": v(-104.35, 76.76) * mm});
            skLineSegment(sketch, "E64.10.1", {"start": v(-107.88, 78.38) * mm, "end": v(-107.43, 79) * mm});
            skLineSegment(sketch, "E64.10.2", {"start": v(-107.88, 78.38) * mm, "end": v(-108.33, 77.76) * mm});
            skLineSegment(sketch, "E64.10.3", {"start": v(-108.33, 77.76) * mm, "end": v(-105.25, 75.53) * mm});
            skLineSegment(sketch, "E64.10.4", {"start": v(-104.8, 76.14) * mm, "end": v(-105.25, 75.53) * mm});
            skLineSegment(sketch, "E64.10.5", {"start": v(-104.8, 76.14) * mm, "end": v(-104.35, 76.76) * mm});
            skLineSegment(sketch, "E64.12.0", {"start": v(-121.51, 54.93) * mm, "end": v(-118.03, 53.38) * mm});
            skLineSegment(sketch, "E64.12.1", {"start": v(-121.82, 54.24) * mm, "end": v(-121.51, 54.93) * mm});
            skLineSegment(sketch, "E64.12.2", {"start": v(-121.82, 54.24) * mm, "end": v(-122.13, 53.54) * mm});
            skLineSegment(sketch, "E64.12.3", {"start": v(-122.13, 53.54) * mm, "end": v(-118.65, 52) * mm});
            skLineSegment(sketch, "E64.12.4", {"start": v(-118.34, 52.69) * mm, "end": v(-118.65, 52) * mm});
            skLineSegment(sketch, "E64.12.5", {"start": v(-118.34, 52.69) * mm, "end": v(-118.03, 53.38) * mm});
            skLineSegment(sketch, "E64.13.0", {"start": v(-126.59, 41.93) * mm, "end": v(-122.96, 40.75) * mm});
            skLineSegment(sketch, "E64.13.1", {"start": v(-126.82, 41.2) * mm, "end": v(-126.59, 41.93) * mm});
            skLineSegment(sketch, "E64.13.2", {"start": v(-126.82, 41.2) * mm, "end": v(-127.06, 40.48) * mm});
            skLineSegment(sketch, "E64.13.3", {"start": v(-127.06, 40.48) * mm, "end": v(-123.44, 39.3) * mm});
            skLineSegment(sketch, "E64.13.4", {"start": v(-123.2, 40.03) * mm, "end": v(-123.44, 39.3) * mm});
            skLineSegment(sketch, "E64.13.5", {"start": v(-123.2, 40.03) * mm, "end": v(-122.96, 40.75) * mm});
            skLineSegment(sketch, "E64.14.0", {"start": v(-130.28, 28.47) * mm, "end": v(-126.55, 27.68) * mm});
            skLineSegment(sketch, "E64.14.1", {"start": v(-130.44, 27.73) * mm, "end": v(-130.28, 28.47) * mm});
            skLineSegment(sketch, "E64.14.2", {"start": v(-130.44, 27.73) * mm, "end": v(-130.6, 26.98) * mm});
            skLineSegment(sketch, "E64.14.3", {"start": v(-130.6, 26.98) * mm, "end": v(-126.87, 26.19) * mm});
            skLineSegment(sketch, "E64.14.4", {"start": v(-126.7, 26.93) * mm, "end": v(-126.87, 26.19) * mm});
            skLineSegment(sketch, "E64.14.5", {"start": v(-126.7, 26.93) * mm, "end": v(-126.55, 27.68) * mm});
            skLineSegment(sketch, "E64.15.0", {"start": v(-132.54, 14.7) * mm, "end": v(-128.75, 14.3) * mm});
            skLineSegment(sketch, "E64.15.1", {"start": v(-132.62, 13.94) * mm, "end": v(-132.54, 14.7) * mm});
            skLineSegment(sketch, "E64.15.2", {"start": v(-132.62, 13.94) * mm, "end": v(-132.7, 13.18) * mm});
            skLineSegment(sketch, "E64.15.3", {"start": v(-132.7, 13.18) * mm, "end": v(-128.91, 12.78) * mm});
            skLineSegment(sketch, "E64.15.4", {"start": v(-128.83, 13.54) * mm, "end": v(-128.91, 12.78) * mm});
            skLineSegment(sketch, "E64.15.5", {"start": v(-128.83, 13.54) * mm, "end": v(-128.75, 14.3) * mm});
            skLineSegment(sketch, "E64.17.0", {"start": v(-132.7, -13.18) * mm, "end": v(-128.91, -12.78) * mm});
            skLineSegment(sketch, "E64.17.1", {"start": v(-132.62, -13.94) * mm, "end": v(-132.7, -13.18) * mm});
            skLineSegment(sketch, "E64.17.2", {"start": v(-132.62, -13.94) * mm, "end": v(-132.54, -14.7) * mm});
            skLineSegment(sketch, "E64.17.3", {"start": v(-132.54, -14.7) * mm, "end": v(-128.75, -14.3) * mm});
            skLineSegment(sketch, "E64.17.4", {"start": v(-128.83, -13.54) * mm, "end": v(-128.75, -14.3) * mm});
            skLineSegment(sketch, "E64.17.5", {"start": v(-128.83, -13.54) * mm, "end": v(-128.91, -12.78) * mm});
            skLineSegment(sketch, "E64.18.0", {"start": v(-130.6, -26.98) * mm, "end": v(-126.87, -26.19) * mm});
            skLineSegment(sketch, "E64.18.1", {"start": v(-130.44, -27.73) * mm, "end": v(-130.6, -26.98) * mm});
            skLineSegment(sketch, "E64.18.2", {"start": v(-130.44, -27.73) * mm, "end": v(-130.28, -28.47) * mm});
            skLineSegment(sketch, "E64.18.3", {"start": v(-130.28, -28.47) * mm, "end": v(-126.55, -27.68) * mm});
            skLineSegment(sketch, "E64.18.4", {"start": v(-126.7, -26.93) * mm, "end": v(-126.55, -27.68) * mm});
            skLineSegment(sketch, "E64.18.5", {"start": v(-126.7, -26.93) * mm, "end": v(-126.87, -26.19) * mm});
            skLineSegment(sketch, "E64.19.0", {"start": v(-127.06, -40.48) * mm, "end": v(-123.44, -39.3) * mm});
            skLineSegment(sketch, "E64.19.1", {"start": v(-126.82, -41.2) * mm, "end": v(-127.06, -40.48) * mm});
            skLineSegment(sketch, "E64.19.2", {"start": v(-126.82, -41.2) * mm, "end": v(-126.59, -41.93) * mm});
            skLineSegment(sketch, "E64.19.3", {"start": v(-126.59, -41.93) * mm, "end": v(-122.96, -40.75) * mm});
            skLineSegment(sketch, "E64.19.4", {"start": v(-123.2, -40.03) * mm, "end": v(-122.96, -40.75) * mm});
            skLineSegment(sketch, "E64.19.5", {"start": v(-123.2, -40.03) * mm, "end": v(-123.44, -39.3) * mm});
            skLineSegment(sketch, "E64.20.0", {"start": v(-122.13, -53.54) * mm, "end": v(-118.65, -52) * mm});
            skLineSegment(sketch, "E64.20.1", {"start": v(-121.82, -54.24) * mm, "end": v(-122.13, -53.54) * mm});
            skLineSegment(sketch, "E64.20.2", {"start": v(-121.82, -54.24) * mm, "end": v(-121.51, -54.93) * mm});
            skLineSegment(sketch, "E64.20.3", {"start": v(-121.51, -54.93) * mm, "end": v(-118.03, -53.38) * mm});
            skLineSegment(sketch, "E64.20.4", {"start": v(-118.34, -52.69) * mm, "end": v(-118.03, -53.38) * mm});
            skLineSegment(sketch, "E64.20.5", {"start": v(-118.34, -52.69) * mm, "end": v(-118.65, -52) * mm});
            skLineSegment(sketch, "E64.22.0", {"start": v(-108.33, -77.76) * mm, "end": v(-105.25, -75.53) * mm});
            skLineSegment(sketch, "E64.22.1", {"start": v(-107.88, -78.38) * mm, "end": v(-108.33, -77.76) * mm});
            skLineSegment(sketch, "E64.22.2", {"start": v(-107.88, -78.38) * mm, "end": v(-107.43, -79) * mm});
            skLineSegment(sketch, "E64.22.3", {"start": v(-107.43, -79) * mm, "end": v(-104.35, -76.76) * mm});
            skLineSegment(sketch, "E64.22.4", {"start": v(-104.8, -76.14) * mm, "end": v(-104.35, -76.76) * mm});
            skLineSegment(sketch, "E64.22.5", {"start": v(-104.8, -76.14) * mm, "end": v(-105.25, -75.53) * mm});
            skLineSegment(sketch, "E64.23.0", {"start": v(-99.6, -88.66) * mm, "end": v(-96.78, -86.11) * mm});
            skLineSegment(sketch, "E64.23.1", {"start": v(-99.1, -89.23) * mm, "end": v(-99.6, -88.66) * mm});
            skLineSegment(sketch, "E64.23.2", {"start": v(-99.1, -89.23) * mm, "end": v(-98.59, -89.8) * mm});
            skLineSegment(sketch, "E64.23.3", {"start": v(-98.59, -89.8) * mm, "end": v(-95.76, -87.25) * mm});
            skLineSegment(sketch, "E64.23.4", {"start": v(-96.27, -86.68) * mm, "end": v(-95.76, -87.25) * mm});
            skLineSegment(sketch, "E64.23.5", {"start": v(-96.27, -86.68) * mm, "end": v(-96.78, -86.11) * mm});
            skLineSegment(sketch, "E64.24.0", {"start": v(-89.8, -98.59) * mm, "end": v(-87.25, -95.76) * mm});
            skLineSegment(sketch, "E64.24.1", {"start": v(-89.23, -99.1) * mm, "end": v(-89.8, -98.59) * mm});
            skLineSegment(sketch, "E64.24.2", {"start": v(-89.23, -99.1) * mm, "end": v(-88.66, -99.6) * mm});
            skLineSegment(sketch, "E64.24.3", {"start": v(-88.66, -99.6) * mm, "end": v(-86.11, -96.78) * mm});
            skLineSegment(sketch, "E64.24.4", {"start": v(-86.68, -96.27) * mm, "end": v(-86.11, -96.78) * mm});
            skLineSegment(sketch, "E64.24.5", {"start": v(-86.68, -96.27) * mm, "end": v(-87.25, -95.76) * mm});
            skLineSegment(sketch, "E64.25.0", {"start": v(-79, -107.43) * mm, "end": v(-76.76, -104.35) * mm});
            skLineSegment(sketch, "E64.25.1", {"start": v(-78.38, -107.88) * mm, "end": v(-79, -107.43) * mm});
            skLineSegment(sketch, "E64.25.2", {"start": v(-78.38, -107.88) * mm, "end": v(-77.76, -108.33) * mm});
            skLineSegment(sketch, "E64.25.3", {"start": v(-77.76, -108.33) * mm, "end": v(-75.53, -105.25) * mm});
            skLineSegment(sketch, "E64.25.4", {"start": v(-76.14, -104.8) * mm, "end": v(-75.53, -105.25) * mm});
            skLineSegment(sketch, "E64.25.5", {"start": v(-76.14, -104.8) * mm, "end": v(-76.76, -104.35) * mm});
            skLineSegment(sketch, "E64.27.0", {"start": v(-54.93, -121.51) * mm, "end": v(-53.38, -118.03) * mm});
            skLineSegment(sketch, "E64.27.1", {"start": v(-54.24, -121.82) * mm, "end": v(-54.93, -121.51) * mm});
            skLineSegment(sketch, "E64.27.2", {"start": v(-54.24, -121.82) * mm, "end": v(-53.54, -122.13) * mm});
            skLineSegment(sketch, "E64.27.3", {"start": v(-53.54, -122.13) * mm, "end": v(-52, -118.65) * mm});
            skLineSegment(sketch, "E64.27.4", {"start": v(-52.69, -118.34) * mm, "end": v(-52, -118.65) * mm});
            skLineSegment(sketch, "E64.27.5", {"start": v(-52.69, -118.34) * mm, "end": v(-53.38, -118.03) * mm});
            skLineSegment(sketch, "E64.28.0", {"start": v(-41.93, -126.59) * mm, "end": v(-40.75, -122.96) * mm});
            skLineSegment(sketch, "E64.28.1", {"start": v(-41.2, -126.82) * mm, "end": v(-41.93, -126.59) * mm});
            skLineSegment(sketch, "E64.28.2", {"start": v(-41.2, -126.82) * mm, "end": v(-40.48, -127.06) * mm});
            skLineSegment(sketch, "E64.28.3", {"start": v(-40.48, -127.06) * mm, "end": v(-39.3, -123.44) * mm});
            skLineSegment(sketch, "E64.28.4", {"start": v(-40.03, -123.2) * mm, "end": v(-39.3, -123.44) * mm});
            skLineSegment(sketch, "E64.28.5", {"start": v(-40.03, -123.2) * mm, "end": v(-40.75, -122.96) * mm});
            skLineSegment(sketch, "E64.29.0", {"start": v(-28.47, -130.28) * mm, "end": v(-27.68, -126.55) * mm});
            skLineSegment(sketch, "E64.29.1", {"start": v(-27.73, -130.44) * mm, "end": v(-28.47, -130.28) * mm});
            skLineSegment(sketch, "E64.29.2", {"start": v(-27.73, -130.44) * mm, "end": v(-26.98, -130.6) * mm});
            skLineSegment(sketch, "E64.29.3", {"start": v(-26.98, -130.6) * mm, "end": v(-26.19, -126.87) * mm});
            skLineSegment(sketch, "E64.29.4", {"start": v(-26.93, -126.7) * mm, "end": v(-26.19, -126.87) * mm});
            skLineSegment(sketch, "E64.29.5", {"start": v(-26.93, -126.7) * mm, "end": v(-27.68, -126.55) * mm});
            skLineSegment(sketch, "E64.30.0", {"start": v(-14.7, -132.54) * mm, "end": v(-14.3, -128.75) * mm});
            skLineSegment(sketch, "E64.30.1", {"start": v(-13.94, -132.62) * mm, "end": v(-14.7, -132.54) * mm});
            skLineSegment(sketch, "E64.30.2", {"start": v(-13.94, -132.62) * mm, "end": v(-13.18, -132.7) * mm});
            skLineSegment(sketch, "E64.30.3", {"start": v(-13.18, -132.7) * mm, "end": v(-12.78, -128.91) * mm});
            skLineSegment(sketch, "E64.30.4", {"start": v(-13.54, -128.83) * mm, "end": v(-12.78, -128.91) * mm});
            skLineSegment(sketch, "E64.30.5", {"start": v(-13.54, -128.83) * mm, "end": v(-14.3, -128.75) * mm});
            skLineSegment(sketch, "E64.32.0", {"start": v(13.18, -132.7) * mm, "end": v(12.78, -128.91) * mm});
            skLineSegment(sketch, "E64.32.1", {"start": v(13.94, -132.62) * mm, "end": v(13.18, -132.7) * mm});
            skLineSegment(sketch, "E64.32.2", {"start": v(13.94, -132.62) * mm, "end": v(14.7, -132.54) * mm});
            skLineSegment(sketch, "E64.32.3", {"start": v(14.7, -132.54) * mm, "end": v(14.3, -128.75) * mm});
            skLineSegment(sketch, "E64.32.4", {"start": v(13.54, -128.83) * mm, "end": v(14.3, -128.75) * mm});
            skLineSegment(sketch, "E64.32.5", {"start": v(13.54, -128.83) * mm, "end": v(12.78, -128.91) * mm});
            skLineSegment(sketch, "E64.33.0", {"start": v(26.98, -130.6) * mm, "end": v(26.19, -126.87) * mm});
            skLineSegment(sketch, "E64.33.1", {"start": v(27.73, -130.44) * mm, "end": v(26.98, -130.6) * mm});
            skLineSegment(sketch, "E64.33.2", {"start": v(27.73, -130.44) * mm, "end": v(28.47, -130.28) * mm});
            skLineSegment(sketch, "E64.33.3", {"start": v(28.47, -130.28) * mm, "end": v(27.68, -126.55) * mm});
            skLineSegment(sketch, "E64.33.4", {"start": v(26.93, -126.7) * mm, "end": v(27.68, -126.55) * mm});
            skLineSegment(sketch, "E64.33.5", {"start": v(26.93, -126.7) * mm, "end": v(26.19, -126.87) * mm});
            skLineSegment(sketch, "E64.34.0", {"start": v(40.48, -127.06) * mm, "end": v(39.3, -123.44) * mm});
            skLineSegment(sketch, "E64.34.1", {"start": v(41.2, -126.82) * mm, "end": v(40.48, -127.06) * mm});
            skLineSegment(sketch, "E64.34.2", {"start": v(41.2, -126.82) * mm, "end": v(41.93, -126.59) * mm});
            skLineSegment(sketch, "E64.34.3", {"start": v(41.93, -126.59) * mm, "end": v(40.75, -122.96) * mm});
            skLineSegment(sketch, "E64.34.4", {"start": v(40.03, -123.2) * mm, "end": v(40.75, -122.96) * mm});
            skLineSegment(sketch, "E64.34.5", {"start": v(40.03, -123.2) * mm, "end": v(39.3, -123.44) * mm});
            skLineSegment(sketch, "E64.35.0", {"start": v(53.54, -122.13) * mm, "end": v(52, -118.65) * mm});
            skLineSegment(sketch, "E64.35.1", {"start": v(54.24, -121.82) * mm, "end": v(53.54, -122.13) * mm});
            skLineSegment(sketch, "E64.35.2", {"start": v(54.24, -121.82) * mm, "end": v(54.93, -121.51) * mm});
            skLineSegment(sketch, "E64.35.3", {"start": v(54.93, -121.51) * mm, "end": v(53.38, -118.03) * mm});
            skLineSegment(sketch, "E64.35.4", {"start": v(52.69, -118.34) * mm, "end": v(53.38, -118.03) * mm});
            skLineSegment(sketch, "E64.35.5", {"start": v(52.69, -118.34) * mm, "end": v(52, -118.65) * mm});
            skLineSegment(sketch, "E64.37.0", {"start": v(77.76, -108.33) * mm, "end": v(75.53, -105.25) * mm});
            skLineSegment(sketch, "E64.37.1", {"start": v(78.38, -107.88) * mm, "end": v(77.76, -108.33) * mm});
            skLineSegment(sketch, "E64.37.2", {"start": v(78.38, -107.88) * mm, "end": v(79, -107.43) * mm});
            skLineSegment(sketch, "E64.37.3", {"start": v(79, -107.43) * mm, "end": v(76.76, -104.35) * mm});
            skLineSegment(sketch, "E64.37.4", {"start": v(76.14, -104.8) * mm, "end": v(76.76, -104.35) * mm});
            skLineSegment(sketch, "E64.37.5", {"start": v(76.14, -104.8) * mm, "end": v(75.53, -105.25) * mm});
            skLineSegment(sketch, "E64.38.0", {"start": v(88.66, -99.6) * mm, "end": v(86.11, -96.78) * mm});
            skLineSegment(sketch, "E64.38.1", {"start": v(89.23, -99.1) * mm, "end": v(88.66, -99.6) * mm});
            skLineSegment(sketch, "E64.38.2", {"start": v(89.23, -99.1) * mm, "end": v(89.8, -98.59) * mm});
            skLineSegment(sketch, "E64.38.3", {"start": v(89.8, -98.59) * mm, "end": v(87.25, -95.76) * mm});
            skLineSegment(sketch, "E64.38.4", {"start": v(86.68, -96.27) * mm, "end": v(87.25, -95.76) * mm});
            skLineSegment(sketch, "E64.38.5", {"start": v(86.68, -96.27) * mm, "end": v(86.11, -96.78) * mm});
            skLineSegment(sketch, "E64.39.0", {"start": v(98.59, -89.8) * mm, "end": v(95.76, -87.25) * mm});
            skLineSegment(sketch, "E64.39.1", {"start": v(99.1, -89.23) * mm, "end": v(98.59, -89.8) * mm});
            skLineSegment(sketch, "E64.39.2", {"start": v(99.1, -89.23) * mm, "end": v(99.6, -88.66) * mm});
            skLineSegment(sketch, "E64.39.3", {"start": v(99.6, -88.66) * mm, "end": v(96.78, -86.11) * mm});
            skLineSegment(sketch, "E64.39.4", {"start": v(96.27, -86.68) * mm, "end": v(96.78, -86.11) * mm});
            skLineSegment(sketch, "E64.39.5", {"start": v(96.27, -86.68) * mm, "end": v(95.76, -87.25) * mm});
            skLineSegment(sketch, "E64.40.0", {"start": v(107.43, -79) * mm, "end": v(104.35, -76.76) * mm});
            skLineSegment(sketch, "E64.40.1", {"start": v(107.88, -78.38) * mm, "end": v(107.43, -79) * mm});
            skLineSegment(sketch, "E64.40.2", {"start": v(107.88, -78.38) * mm, "end": v(108.33, -77.76) * mm});
            skLineSegment(sketch, "E64.40.3", {"start": v(108.33, -77.76) * mm, "end": v(105.25, -75.53) * mm});
            skLineSegment(sketch, "E64.40.4", {"start": v(104.8, -76.14) * mm, "end": v(105.25, -75.53) * mm});
            skLineSegment(sketch, "E64.40.5", {"start": v(104.8, -76.14) * mm, "end": v(104.35, -76.76) * mm});
            skLineSegment(sketch, "E64.42.0", {"start": v(121.51, -54.93) * mm, "end": v(118.03, -53.38) * mm});
            skLineSegment(sketch, "E64.42.1", {"start": v(121.82, -54.24) * mm, "end": v(121.51, -54.93) * mm});
            skLineSegment(sketch, "E64.42.2", {"start": v(121.82, -54.24) * mm, "end": v(122.13, -53.54) * mm});
            skLineSegment(sketch, "E64.42.3", {"start": v(122.13, -53.54) * mm, "end": v(118.65, -52) * mm});
            skLineSegment(sketch, "E64.42.4", {"start": v(118.34, -52.69) * mm, "end": v(118.65, -52) * mm});
            skLineSegment(sketch, "E64.42.5", {"start": v(118.34, -52.69) * mm, "end": v(118.03, -53.38) * mm});
            skLineSegment(sketch, "E64.43.0", {"start": v(126.59, -41.93) * mm, "end": v(122.96, -40.75) * mm});
            skLineSegment(sketch, "E64.43.1", {"start": v(126.82, -41.2) * mm, "end": v(126.59, -41.93) * mm});
            skLineSegment(sketch, "E64.43.2", {"start": v(126.82, -41.2) * mm, "end": v(127.06, -40.48) * mm});
            skLineSegment(sketch, "E64.43.3", {"start": v(127.06, -40.48) * mm, "end": v(123.44, -39.3) * mm});
            skLineSegment(sketch, "E64.43.4", {"start": v(123.2, -40.03) * mm, "end": v(123.44, -39.3) * mm});
            skLineSegment(sketch, "E64.43.5", {"start": v(123.2, -40.03) * mm, "end": v(122.96, -40.75) * mm});
            skLineSegment(sketch, "E64.44.0", {"start": v(130.28, -28.47) * mm, "end": v(126.55, -27.68) * mm});
            skLineSegment(sketch, "E64.44.1", {"start": v(130.44, -27.73) * mm, "end": v(130.28, -28.47) * mm});
            skLineSegment(sketch, "E64.44.2", {"start": v(130.44, -27.73) * mm, "end": v(130.6, -26.98) * mm});
            skLineSegment(sketch, "E64.44.3", {"start": v(130.6, -26.98) * mm, "end": v(126.87, -26.19) * mm});
            skLineSegment(sketch, "E64.44.4", {"start": v(126.7, -26.93) * mm, "end": v(126.87, -26.19) * mm});
            skLineSegment(sketch, "E64.44.5", {"start": v(126.7, -26.93) * mm, "end": v(126.55, -27.68) * mm});
            skLineSegment(sketch, "E64.45.0", {"start": v(132.54, -14.7) * mm, "end": v(128.75, -14.3) * mm});
            skLineSegment(sketch, "E64.45.1", {"start": v(132.62, -13.94) * mm, "end": v(132.54, -14.7) * mm});
            skLineSegment(sketch, "E64.45.2", {"start": v(132.62, -13.94) * mm, "end": v(132.7, -13.18) * mm});
            skLineSegment(sketch, "E64.45.3", {"start": v(132.7, -13.18) * mm, "end": v(128.91, -12.78) * mm});
            skLineSegment(sketch, "E64.45.4", {"start": v(128.83, -13.54) * mm, "end": v(128.91, -12.78) * mm});
            skLineSegment(sketch, "E64.45.5", {"start": v(128.83, -13.54) * mm, "end": v(128.75, -14.3) * mm});
            skLineSegment(sketch, "E64.47.0", {"start": v(132.7, 13.18) * mm, "end": v(128.91, 12.78) * mm});
            skLineSegment(sketch, "E64.47.1", {"start": v(132.62, 13.94) * mm, "end": v(132.7, 13.18) * mm});
            skLineSegment(sketch, "E64.47.2", {"start": v(132.62, 13.94) * mm, "end": v(132.54, 14.7) * mm});
            skLineSegment(sketch, "E64.47.3", {"start": v(132.54, 14.7) * mm, "end": v(128.75, 14.3) * mm});
            skLineSegment(sketch, "E64.47.4", {"start": v(128.83, 13.54) * mm, "end": v(128.75, 14.3) * mm});
            skLineSegment(sketch, "E64.47.5", {"start": v(128.83, 13.54) * mm, "end": v(128.91, 12.78) * mm});
            skLineSegment(sketch, "E64.48.0", {"start": v(130.6, 26.98) * mm, "end": v(126.87, 26.19) * mm});
            skLineSegment(sketch, "E64.48.1", {"start": v(130.44, 27.73) * mm, "end": v(130.6, 26.98) * mm});
            skLineSegment(sketch, "E64.48.2", {"start": v(130.44, 27.73) * mm, "end": v(130.28, 28.47) * mm});
            skLineSegment(sketch, "E64.48.3", {"start": v(130.28, 28.47) * mm, "end": v(126.55, 27.68) * mm});
            skLineSegment(sketch, "E64.48.4", {"start": v(126.7, 26.93) * mm, "end": v(126.55, 27.68) * mm});
            skLineSegment(sketch, "E64.48.5", {"start": v(126.7, 26.93) * mm, "end": v(126.87, 26.19) * mm});
            skLineSegment(sketch, "E64.49.0", {"start": v(127.06, 40.48) * mm, "end": v(123.44, 39.3) * mm});
            skLineSegment(sketch, "E64.49.1", {"start": v(126.82, 41.2) * mm, "end": v(127.06, 40.48) * mm});
            skLineSegment(sketch, "E64.49.2", {"start": v(126.82, 41.2) * mm, "end": v(126.59, 41.93) * mm});
            skLineSegment(sketch, "E64.49.3", {"start": v(126.59, 41.93) * mm, "end": v(122.96, 40.75) * mm});
            skLineSegment(sketch, "E64.49.4", {"start": v(123.2, 40.03) * mm, "end": v(122.96, 40.75) * mm});
            skLineSegment(sketch, "E64.49.5", {"start": v(123.2, 40.03) * mm, "end": v(123.44, 39.3) * mm});
            skLineSegment(sketch, "E64.50.0", {"start": v(122.13, 53.54) * mm, "end": v(118.65, 52) * mm});
            skLineSegment(sketch, "E64.50.1", {"start": v(121.82, 54.24) * mm, "end": v(122.13, 53.54) * mm});
            skLineSegment(sketch, "E64.50.2", {"start": v(121.82, 54.24) * mm, "end": v(121.51, 54.93) * mm});
            skLineSegment(sketch, "E64.50.3", {"start": v(121.51, 54.93) * mm, "end": v(118.03, 53.38) * mm});
            skLineSegment(sketch, "E64.50.4", {"start": v(118.34, 52.69) * mm, "end": v(118.03, 53.38) * mm});
            skLineSegment(sketch, "E64.50.5", {"start": v(118.34, 52.69) * mm, "end": v(118.65, 52) * mm});
            skLineSegment(sketch, "E64.52.0", {"start": v(108.33, 77.76) * mm, "end": v(105.25, 75.53) * mm});
            skLineSegment(sketch, "E64.52.1", {"start": v(107.88, 78.38) * mm, "end": v(108.33, 77.76) * mm});
            skLineSegment(sketch, "E64.52.2", {"start": v(107.88, 78.38) * mm, "end": v(107.43, 79) * mm});
            skLineSegment(sketch, "E64.52.3", {"start": v(107.43, 79) * mm, "end": v(104.35, 76.76) * mm});
            skLineSegment(sketch, "E64.52.4", {"start": v(104.8, 76.14) * mm, "end": v(104.35, 76.76) * mm});
            skLineSegment(sketch, "E64.52.5", {"start": v(104.8, 76.14) * mm, "end": v(105.25, 75.53) * mm});
            skLineSegment(sketch, "E64.53.0", {"start": v(99.6, 88.66) * mm, "end": v(96.78, 86.11) * mm});
            skLineSegment(sketch, "E64.53.1", {"start": v(99.1, 89.23) * mm, "end": v(99.6, 88.66) * mm});
            skLineSegment(sketch, "E64.53.2", {"start": v(99.1, 89.23) * mm, "end": v(98.59, 89.8) * mm});
            skLineSegment(sketch, "E64.53.3", {"start": v(98.59, 89.8) * mm, "end": v(95.76, 87.25) * mm});
            skLineSegment(sketch, "E64.53.4", {"start": v(96.27, 86.68) * mm, "end": v(95.76, 87.25) * mm});
            skLineSegment(sketch, "E64.53.5", {"start": v(96.27, 86.68) * mm, "end": v(96.78, 86.11) * mm});
            skLineSegment(sketch, "E64.54.0", {"start": v(89.8, 98.59) * mm, "end": v(87.25, 95.76) * mm});
            skLineSegment(sketch, "E64.54.1", {"start": v(89.23, 99.1) * mm, "end": v(89.8, 98.59) * mm});
            skLineSegment(sketch, "E64.54.2", {"start": v(89.23, 99.1) * mm, "end": v(88.66, 99.6) * mm});
            skLineSegment(sketch, "E64.54.3", {"start": v(88.66, 99.6) * mm, "end": v(86.11, 96.78) * mm});
            skLineSegment(sketch, "E64.54.4", {"start": v(86.68, 96.27) * mm, "end": v(86.11, 96.78) * mm});
            skLineSegment(sketch, "E64.54.5", {"start": v(86.68, 96.27) * mm, "end": v(87.25, 95.76) * mm});
            skLineSegment(sketch, "E64.55.0", {"start": v(79, 107.43) * mm, "end": v(76.76, 104.35) * mm});
            skLineSegment(sketch, "E64.55.1", {"start": v(78.38, 107.88) * mm, "end": v(79, 107.43) * mm});
            skLineSegment(sketch, "E64.55.2", {"start": v(78.38, 107.88) * mm, "end": v(77.76, 108.33) * mm});
            skLineSegment(sketch, "E64.55.3", {"start": v(77.76, 108.33) * mm, "end": v(75.53, 105.25) * mm});
            skLineSegment(sketch, "E64.55.4", {"start": v(76.14, 104.8) * mm, "end": v(75.53, 105.25) * mm});
            skLineSegment(sketch, "E64.55.5", {"start": v(76.14, 104.8) * mm, "end": v(76.76, 104.35) * mm});
            skLineSegment(sketch, "E64.57.0", {"start": v(54.93, 121.51) * mm, "end": v(53.38, 118.03) * mm});
            skLineSegment(sketch, "E64.57.1", {"start": v(54.24, 121.82) * mm, "end": v(54.93, 121.51) * mm});
            skLineSegment(sketch, "E64.57.2", {"start": v(54.24, 121.82) * mm, "end": v(53.54, 122.13) * mm});
            skLineSegment(sketch, "E64.57.3", {"start": v(53.54, 122.13) * mm, "end": v(52, 118.65) * mm});
            skLineSegment(sketch, "E64.57.4", {"start": v(52.69, 118.34) * mm, "end": v(52, 118.65) * mm});
            skLineSegment(sketch, "E64.57.5", {"start": v(52.69, 118.34) * mm, "end": v(53.38, 118.03) * mm});
            skPoint(sketch, "E64.center", {"position": v(0, 0) * mm});
            skLineSegment(sketch, "E65.2.58.0", {"start": v(41.93, 126.59) * mm, "end": v(40.75, 122.96) * mm});
            skLineSegment(sketch, "E65.3.58.0", {"start": v(41.2, 126.82) * mm, "end": v(41.93, 126.59) * mm});
            skLineSegment(sketch, "E65.6.58.0", {"start": v(41.2, 126.82) * mm, "end": v(40.48, 127.06) * mm});
            skLineSegment(sketch, "E65.9.58.0", {"start": v(40.48, 127.06) * mm, "end": v(39.3, 123.44) * mm});
            skLineSegment(sketch, "E65.12.58.0", {"start": v(40.03, 123.2) * mm, "end": v(39.3, 123.44) * mm});
            skLineSegment(sketch, "E65.15.58.0", {"start": v(40.03, 123.2) * mm, "end": v(40.75, 122.96) * mm});
            skLineSegment(sketch, "E65.2.59.0", {"start": v(28.47, 130.28) * mm, "end": v(27.68, 126.55) * mm});
            skLineSegment(sketch, "E65.3.59.0", {"start": v(27.73, 130.44) * mm, "end": v(28.47, 130.28) * mm});
            skLineSegment(sketch, "E65.6.59.0", {"start": v(27.73, 130.44) * mm, "end": v(26.98, 130.6) * mm});
            skLineSegment(sketch, "E65.9.59.0", {"start": v(26.98, 130.6) * mm, "end": v(26.19, 126.87) * mm});
            skLineSegment(sketch, "E65.12.59.0", {"start": v(26.93, 126.7) * mm, "end": v(26.19, 126.87) * mm});
            skLineSegment(sketch, "E65.15.59.0", {"start": v(26.93, 126.7) * mm, "end": v(27.68, 126.55) * mm});
            skSolve(sketch);
        }
        {
            var Q0;
            Q0=qSketchRegion(id+"F25",true);
            extrude(context, id + "F26", {"entities" : qUnion([Q0]), "operationType" : NewBodyOperationType.ADD, "depth" : 2.54 * mm});
        }
    });
